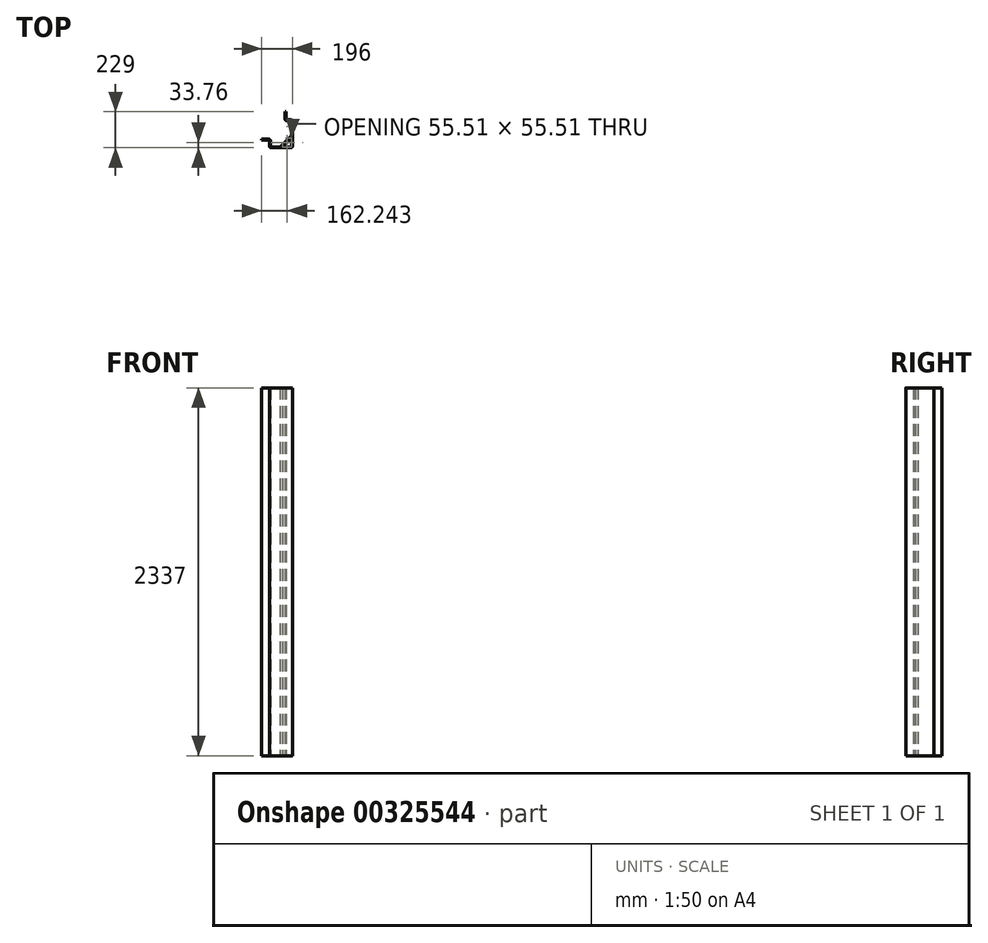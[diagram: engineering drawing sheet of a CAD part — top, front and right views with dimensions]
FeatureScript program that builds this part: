
annotation { "Feature Type Name" : "Feature", "Feature Type Description" : "" }
export const myFeature = defineFeature(function(context is Context, id is Id, definition is map)
    precondition{}
    {
        {
            var Q0;
            Q0=qCreatedBy(makeId("Top.planeOp"),FACE);
            var sketch = newSketch(context, id + "F0", { "sketchPlane" : qUnion([Q0])});
            skLineSegment(sketch, "E0", {"start": v(-46, 83.28) * mm, "end": v(-46, 36.28) * mm});
            skLineSegment(sketch, "E1", {"start": v(-46, 83.28) * mm, "end": v(-40, 83.28) * mm});
            skLineSegment(sketch, "E2", {"start": v(-40, 83.28) * mm, "end": v(-40, 37.28) * mm});
            skLineSegment(sketch, "E3", {"start": v(-35, 32.28) * mm, "end": v(-11, 32.28) * mm});
            skLineSegment(sketch, "E4", {"start": v(0, 21.28) * mm, "end": v(0, -134.72) * mm});
            skLineSegment(sketch, "E5", {"start": v(-11, -145.72) * mm, "end": v(-135, -145.72) * mm});
            skLineSegment(sketch, "E6", {"start": v(-146, -134.72) * mm, "end": v(-146, -100.72) * mm});
            skLineSegment(sketch, "E7", {"start": v(-151, -95.72) * mm, "end": v(-196, -95.72) * mm});
            skLineSegment(sketch, "E8", {"start": v(-196, -95.72) * mm, "end": v(-196, -89.72) * mm});
            skLineSegment(sketch, "E9", {"start": v(-196, -89.72) * mm, "end": v(-151, -89.72) * mm});
            skLineSegment(sketch, "E10", {"start": v(-140, -100.72) * mm, "end": v(-140, -134.72) * mm});
            skLineSegment(sketch, "E11", {"start": v(-135, -139.72) * mm, "end": v(-11, -139.72) * mm});
            skLineSegment(sketch, "E12", {"start": v(-6, -134.72) * mm, "end": v(-6, 21.28) * mm});
            skLineSegment(sketch, "E13", {"start": v(-11, 26.28) * mm, "end": v(-36, 26.28) * mm});
            skLineSegment(sketch, "E14.0", {"start": v(-61.51, -139.72) * mm, "end": v(-6, -84.2) * mm});
            skLineSegment(sketch, "E15.0", {"start": v(-78.49, -139.72) * mm, "end": v(-6, -67.23) * mm});
            skPoint(sketch, "E16.visualSharp", {"position": v(-146, -95.72) * mm});
            skArc(sketch, "E16.filletArc", {"start": v(-146, -100.72) * mm, "mid": v(-147.46, -97.18) * mm, "end": v(-151, -95.72) * mm});
            skPoint(sketch, "E17.visualSharp", {"position": v(-140, -139.72) * mm});
            skArc(sketch, "E17.filletArc", {"start": v(-140, -134.72) * mm, "mid": v(-138.54, -138.25) * mm, "end": v(-135, -139.72) * mm});
            skPoint(sketch, "E18.visualSharp", {"position": v(-6, -139.72) * mm});
            skArc(sketch, "E18.filletArc", {"start": v(-11, -139.72) * mm, "mid": v(-7.46, -138.25) * mm, "end": v(-6, -134.72) * mm});
            skPoint(sketch, "E19.visualSharp", {"position": v(-6, 26.28) * mm});
            skArc(sketch, "E19.filletArc", {"start": v(-6, 21.28) * mm, "mid": v(-7.46, 24.82) * mm, "end": v(-11, 26.28) * mm});
            skPoint(sketch, "E20.visualSharp", {"position": v(-40, 32.28) * mm});
            skArc(sketch, "E20.filletArc", {"start": v(-40, 37.28) * mm, "mid": v(-38.54, 33.75) * mm, "end": v(-35, 32.28) * mm});
            skPoint(sketch, "E21.visualSharp", {"position": v(-46, 26.28) * mm});
            skArc(sketch, "E21.filletArc", {"start": v(-46, 36.28) * mm, "mid": v(-43.07, 29.21) * mm, "end": v(-36, 26.28) * mm});
            skPoint(sketch, "E22.visualSharp", {"position": v(0, 32.28) * mm});
            skArc(sketch, "E22.filletArc", {"start": v(0, 21.28) * mm, "mid": v(-3.22, 29.06) * mm, "end": v(-11, 32.28) * mm});
            skPoint(sketch, "E23.visualSharp", {"position": v(0, -145.72) * mm});
            skArc(sketch, "E23.filletArc", {"start": v(-11, -145.72) * mm, "mid": v(-3.22, -142.5) * mm, "end": v(0, -134.72) * mm});
            skPoint(sketch, "E24.visualSharp", {"position": v(-146, -145.72) * mm});
            skArc(sketch, "E24.filletArc", {"start": v(-146, -134.72) * mm, "mid": v(-142.78, -142.5) * mm, "end": v(-135, -145.72) * mm});
            skPoint(sketch, "E25.visualSharp", {"position": v(-140, -89.72) * mm});
            skArc(sketch, "E25.filletArc", {"start": v(-140, -100.72) * mm, "mid": v(-143.22, -92.94) * mm, "end": v(-151, -89.72) * mm});
            skSolve(sketch);
        }
        {
            var Q0;
            {var subQ0=sQuery(id+"F0.wireOp",EDGE,"E14.0");Q0=makeQuery(id+"F0.imprint","IMPRINT",FACE,{"disambiguationData":[TD([[makeQuery(id+"F0.imprint","IMPRINT",EDGE,{"derivedFrom":subQ0}),1.0]])]});}
            var Q1;
            Q1=makeQuery(id+"F0.imprint","IMPRINT",FACE,{"disambiguationData":[TD([[makeQuery(id+"F0.imprint","IMPRINT",EDGE,{"derivedFrom":sQuery(id+"F0.wireOp",EDGE,"E0")}),1.0]])]});
            extrude(context, id + "F1", {"entities" : qUnion([Q0, Q1]), "depth" : 2337 * mm});
        }
    });
